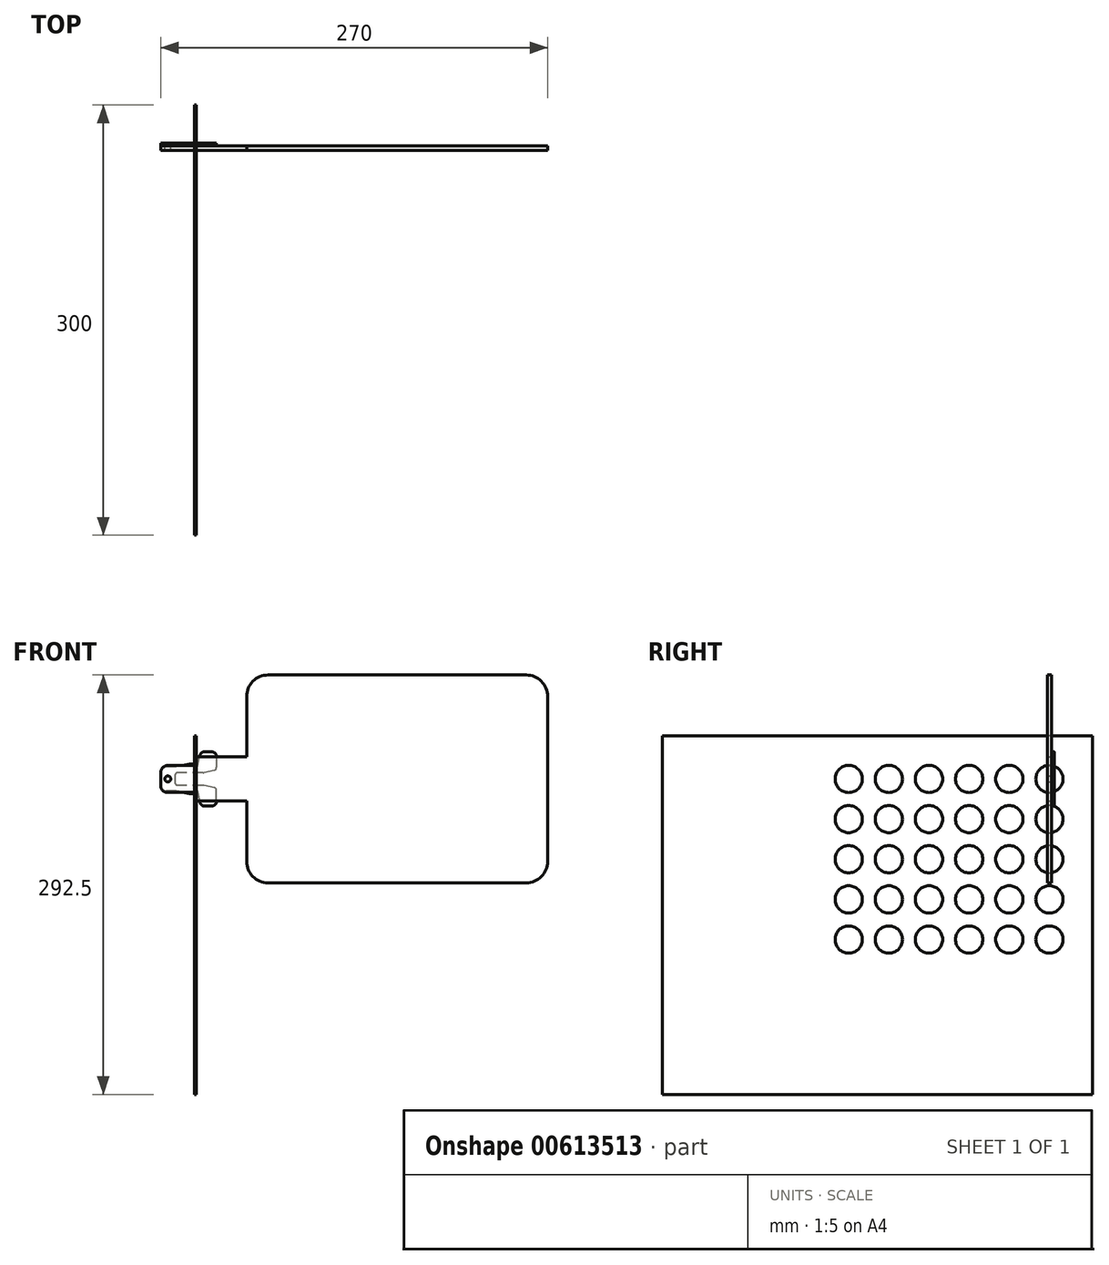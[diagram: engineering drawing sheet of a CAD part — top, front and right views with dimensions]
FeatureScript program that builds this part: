
annotation { "Feature Type Name" : "Feature", "Feature Type Description" : "" }
export const myFeature = defineFeature(function(context is Context, id is Id, definition is map)
    precondition{}
    {
        {
            var Q0;
            Q0=qCreatedBy(makeId("Front.planeOp"),FACE);
            var sketch = newSketch(context, id + "F0", { "sketchPlane" : qUnion([Q0])});
            skLineSegment(sketch, "E0.bottom", {"start": v(90, -72.5) * mm, "end": v(-90, -72.5) * mm});
            skLineSegment(sketch, "E0.top", {"start": v(90, 72.5) * mm, "end": v(-90, 72.5) * mm});
            skLineSegment(sketch, "E0.left", {"start": v(105, -57.5) * mm, "end": v(105, 57.5) * mm});
            skLineSegment(sketch, "E0.right", {"start": v(-105, -57.5) * mm, "end": v(-105, -15.4) * mm});
            skPoint(sketch, "E0.middle", {"position": v(0, 0) * mm});
            skPoint(sketch, "E1.visualSharp", {"position": v(-105, 72.5) * mm});
            skArc(sketch, "E1.filletArc", {"start": v(-90, 72.5) * mm, "mid": v(-100.6, 68.1) * mm, "end": v(-105, 57.5) * mm});
            skPoint(sketch, "E2.visualSharp", {"position": v(105, 72.5) * mm});
            skArc(sketch, "E2.filletArc", {"start": v(105, 57.5) * mm, "mid": v(100.6, 68.1) * mm, "end": v(90, 72.5) * mm});
            skPoint(sketch, "E3.visualSharp", {"position": v(105, -72.5) * mm});
            skArc(sketch, "E3.filletArc", {"start": v(90, -72.5) * mm, "mid": v(100.6, -68.1) * mm, "end": v(105, -57.5) * mm});
            skPoint(sketch, "E4.visualSharp", {"position": v(-105, -72.5) * mm});
            skArc(sketch, "E4.filletArc", {"start": v(-105, -57.5) * mm, "mid": v(-100.6, -68.1) * mm, "end": v(-90, -72.5) * mm});
            skLineSegment(sketch, "E5", {"start": v(-165, 0) * mm, "end": v(-165, -4.4) * mm});
            skLineSegment(sketch, "E6", {"start": v(-160, -9.4) * mm, "end": v(-140, -9.4) * mm});
            skLineSegment(sketch, "E7", {"start": v(-140, -9.4) * mm, "end": v(-140, -15.4) * mm});
            skLineSegment(sketch, "E8", {"start": v(-140, -15.4) * mm, "end": v(-105, -15.4) * mm});
            skLineSegment(sketch, "E9.MirrorCS", {"start": v(-140, 15.4) * mm, "end": v(-105, 15.4) * mm});
            skLineSegment(sketch, "E10.MirrorCS", {"start": v(-140, 9.4) * mm, "end": v(-140, 15.4) * mm});
            skLineSegment(sketch, "E11.MirrorCS", {"start": v(-160, 9.4) * mm, "end": v(-140, 9.4) * mm});
            skLineSegment(sketch, "E12.MirrorCS", {"start": v(-165, 0) * mm, "end": v(-165, 4.4) * mm});
            skLineSegment(sketch, "E13.trimOffspring", {"start": v(-105, 15.4) * mm, "end": v(-105, 57.5) * mm});
            skCircle(sketch, "E14", {"center": v(-160, 0) * mm, "radius": 2.1 * mm});
            skPoint(sketch, "E15.visualSharp", {"position": v(-165, 9.4) * mm});
            skArc(sketch, "E15.filletArc", {"start": v(-160, 9.4) * mm, "mid": v(-163.54, 7.94) * mm, "end": v(-165, 4.4) * mm});
            skPoint(sketch, "E16.visualSharp", {"position": v(-165, -9.4) * mm});
            skArc(sketch, "E16.filletArc", {"start": v(-165, -4.4) * mm, "mid": v(-163.54, -7.94) * mm, "end": v(-160, -9.4) * mm});
            skSolve(sketch);
        }
        {
            var Q0;
            Q0=makeQuery(id+"F0.imprint","IMPRINT",FACE,{"disambiguationData":[TD([[makeQuery(id+"F0.imprint","IMPRINT",EDGE,{"derivedFrom":sQuery(id+"F0.wireOp",EDGE,"E0.bottom")}),-1.0]])]});
            extrude(context, id + "F1", {"entities" : qUnion([Q0]), "depth" : 3 * mm, "offsetDistance" : 25 * mm, "symmetric" : true});
        }
        {
            var Q0;
            Q0=makeQuery(id+"F1.opExtrude","SWEPT_FACE",FACE,{"disambiguationData":[OSD([sQuery(id+"F0.wireOp",EDGE,"E10.MirrorCS")])]});
            cPlane(context, id + "F2", {"entities" : qUnion([Q0]), "cplaneType" : CPlaneType.OFFSET, "offset" : 0 * mm, "width" : 150 * mm, "height" : 150 * mm});
        }
        {
            var Q0;
            Q0=qCreatedBy(id+"F2.planeOp",FACE);
            var sketch = newSketch(context, id + "F3", { "sketchPlane" : qUnion([Q0])});
            skCircle(sketch, "E17", {"center": v(0, 0) * mm, "radius": 9.5 * mm});
            skLineSegment(sketch, "E18.bottom", {"start": v(-30, 30) * mm, "end": v(270, 30) * mm});
            skLineSegment(sketch, "E18.top", {"start": v(-30, -220) * mm, "end": v(270, -220) * mm});
            skLineSegment(sketch, "E18.left", {"start": v(-30, 30) * mm, "end": v(-30, -220) * mm});
            skLineSegment(sketch, "E18.right", {"start": v(270, 30) * mm, "end": v(270, -220) * mm});
            skCircle(sketch, "E19.0.1.0", {"center": v(0, -28) * mm, "radius": 9.5 * mm});
            skCircle(sketch, "E19.0.2.0", {"center": v(0, -56) * mm, "radius": 9.5 * mm});
            skCircle(sketch, "E19.0.3.0", {"center": v(0, -84) * mm, "radius": 9.5 * mm});
            skCircle(sketch, "E19.0.4.0", {"center": v(0, -112) * mm, "radius": 9.5 * mm});
            skCircle(sketch, "E19.1.0.0", {"center": v(28, 0) * mm, "radius": 9.5 * mm});
            skCircle(sketch, "E19.1.1.0", {"center": v(28, -28) * mm, "radius": 9.5 * mm});
            skCircle(sketch, "E19.1.2.0", {"center": v(28, -56) * mm, "radius": 9.5 * mm});
            skCircle(sketch, "E19.1.3.0", {"center": v(28, -84) * mm, "radius": 9.5 * mm});
            skCircle(sketch, "E19.1.4.0", {"center": v(28, -112) * mm, "radius": 9.5 * mm});
            skCircle(sketch, "E19.2.0.0", {"center": v(56, 0) * mm, "radius": 9.5 * mm});
            skCircle(sketch, "E19.2.1.0", {"center": v(56, -28) * mm, "radius": 9.5 * mm});
            skCircle(sketch, "E19.2.2.0", {"center": v(56, -56) * mm, "radius": 9.5 * mm});
            skCircle(sketch, "E19.2.3.0", {"center": v(56, -84) * mm, "radius": 9.5 * mm});
            skCircle(sketch, "E19.2.4.0", {"center": v(56, -112) * mm, "radius": 9.5 * mm});
            skCircle(sketch, "E19.3.0.0", {"center": v(84, 0) * mm, "radius": 9.5 * mm});
            skCircle(sketch, "E19.3.1.0", {"center": v(84, -28) * mm, "radius": 9.5 * mm});
            skCircle(sketch, "E19.3.2.0", {"center": v(84, -56) * mm, "radius": 9.5 * mm});
            skCircle(sketch, "E19.3.3.0", {"center": v(84, -84) * mm, "radius": 9.5 * mm});
            skCircle(sketch, "E19.3.4.0", {"center": v(84, -112) * mm, "radius": 9.5 * mm});
            skCircle(sketch, "E19.4.0.0", {"center": v(112, 0) * mm, "radius": 9.5 * mm});
            skCircle(sketch, "E19.4.1.0", {"center": v(112, -28) * mm, "radius": 9.5 * mm});
            skCircle(sketch, "E19.4.2.0", {"center": v(112, -56) * mm, "radius": 9.5 * mm});
            skCircle(sketch, "E19.4.3.0", {"center": v(112, -84) * mm, "radius": 9.5 * mm});
            skCircle(sketch, "E19.4.4.0", {"center": v(112, -112) * mm, "radius": 9.5 * mm});
            skCircle(sketch, "E19.5.0.0", {"center": v(140, 0) * mm, "radius": 9.5 * mm});
            skCircle(sketch, "E19.5.1.0", {"center": v(140, -28) * mm, "radius": 9.5 * mm});
            skCircle(sketch, "E19.5.2.0", {"center": v(140, -56) * mm, "radius": 9.5 * mm});
            skCircle(sketch, "E19.5.3.0", {"center": v(140, -84) * mm, "radius": 9.5 * mm});
            skCircle(sketch, "E19.5.4.0", {"center": v(140, -112) * mm, "radius": 9.5 * mm});
            skLineSegment(sketch, "E19.direction1", {"start": v(0, 0) * mm, "end": v(28, 0) * mm, "construction": true});
            skLineSegment(sketch, "E19.direction2", {"start": v(0, 0) * mm, "end": v(0, -28) * mm, "construction": true});
            skSolve(sketch);
        }
        {
            var Q0;
            Q0=qSketchRegion(id+"F3",true);
            extrude(context, id + "F4", {"entities" : qUnion([Q0]), "depth" : 1.5 * mm, "offsetDistance" : 25 * mm});
        }
        {
            var Q0;
            Q0=makeQuery(id+"F1.opExtrude","CAP_FACE",FACE,{"disambiguationData":[OSD([sQuery(id+"F0.wireOp",EDGE,"E0.bottom"),sQuery(id+"F0.wireOp",EDGE,"E0.top"),sQuery(id+"F0.wireOp",EDGE,"E0.left"),sQuery(id+"F0.wireOp",EDGE,"E0.right"),sQuery(id+"F0.wireOp",EDGE,"E1.filletArc"),sQuery(id+"F0.wireOp",EDGE,"E2.filletArc"),sQuery(id+"F0.wireOp",EDGE,"E3.filletArc"),sQuery(id+"F0.wireOp",EDGE,"E4.filletArc"),sQuery(id+"F0.wireOp",EDGE,"E5"),sQuery(id+"F0.wireOp",EDGE,"E6"),sQuery(id+"F0.wireOp",EDGE,"E7"),sQuery(id+"F0.wireOp",EDGE,"E8"),sQuery(id+"F0.wireOp",EDGE,"E9.MirrorCS"),sQuery(id+"F0.wireOp",EDGE,"E10.MirrorCS"),sQuery(id+"F0.wireOp",EDGE,"E11.MirrorCS"),sQuery(id+"F0.wireOp",EDGE,"E12.MirrorCS"),sQuery(id+"F0.wireOp",EDGE,"E13.trimOffspring"),sQuery(id+"F0.wireOp",EDGE,"E14")])],"isStart":true});
            var sketch = newSketch(context, id + "F5", { "sketchPlane" : qUnion([Q0])});
            skLineSegment(sketch, "E20", {"start": v(139.5, 7.9) * mm, "end": v(141.5, 7.9) * mm});
            skLineSegment(sketch, "E21", {"start": v(141.5, 7.9) * mm, "end": v(142, 10.4) * mm});
            skLineSegment(sketch, "E22", {"start": v(142, 10.4) * mm, "end": v(145, 10.4) * mm});
            skLineSegment(sketch, "E23", {"start": v(139.5, 7.9) * mm, "end": v(137.56, 16.42) * mm});
            skLineSegment(sketch, "E24", {"start": v(134.46, 18.9) * mm, "end": v(129.3, 18.9) * mm});
            skLineSegment(sketch, "E25", {"start": v(126, 15.6) * mm, "end": v(126, 8) * mm});
            skLineSegment(sketch, "E26", {"start": v(127.57, 6.05) * mm, "end": v(134.79, 4.45) * mm});
            skLineSegment(sketch, "E27", {"start": v(135.22, 4.4) * mm, "end": v(153, 4.4) * mm});
            skLineSegment(sketch, "E28", {"start": v(155, 2.4) * mm, "end": v(155, 0) * mm});
            skArc(sketch, "E29", {"start": v(129.3, 18.9) * mm, "mid": v(126.97, 17.93) * mm, "end": v(126, 15.6) * mm});
            skArc(sketch, "E30", {"start": v(137.56, 16.42) * mm, "mid": v(136.44, 18.2) * mm, "end": v(134.46, 18.9) * mm});
            skPoint(sketch, "E31.orphan", {"position": v(137, 18.9) * mm});
            skCircle(sketch, "E32.0", {"center": v(160, 0) * mm, "radius": 2.1 * mm});
            skPoint(sketch, "E33.visualSharp", {"position": v(126, 6.4) * mm});
            skArc(sketch, "E33.filletArc", {"start": v(126, 8) * mm, "mid": v(126.44, 6.75) * mm, "end": v(127.57, 6.05) * mm});
            skPoint(sketch, "E34.visualSharp", {"position": v(155, 4.4) * mm});
            skArc(sketch, "E34.filletArc", {"start": v(155, 2.4) * mm, "mid": v(154.41, 3.81) * mm, "end": v(153, 4.4) * mm});
            skPoint(sketch, "E35.visualSharp", {"position": v(135, 4.4) * mm});
            skArc(sketch, "E35.filletArc", {"start": v(134.79, 4.45) * mm, "mid": v(135, 4.41) * mm, "end": v(135.22, 4.4) * mm});
            skLineSegment(sketch, "E36", {"start": v(145, 10.4) * mm, "end": v(154, 8.4) * mm});
            skLineSegment(sketch, "E37", {"start": v(154, 8.4) * mm, "end": v(161, 8.4) * mm});
            skLineSegment(sketch, "E38", {"start": v(165, 4.4) * mm, "end": v(165, 0) * mm});
            skPoint(sketch, "E39.visualSharp", {"position": v(165, 8.4) * mm});
            skArc(sketch, "E39.filletArc", {"start": v(165, 4.4) * mm, "mid": v(163.83, 7.23) * mm, "end": v(161, 8.4) * mm});
            skLineSegment(sketch, "E40.MirrorCS", {"start": v(155, -2.4) * mm, "end": v(155, 0) * mm});
            skArc(sketch, "E41.MirrorCS", {"start": v(155, -2.4) * mm, "mid": v(154.41, -3.81) * mm, "end": v(153, -4.4) * mm});
            skLineSegment(sketch, "E42.MirrorCS", {"start": v(135.22, -4.4) * mm, "end": v(153, -4.4) * mm});
            skArc(sketch, "E43.MirrorCS", {"start": v(134.79, -4.45) * mm, "mid": v(135, -4.41) * mm, "end": v(135.22, -4.4) * mm});
            skLineSegment(sketch, "E44.MirrorCS", {"start": v(127.57, -6.05) * mm, "end": v(134.79, -4.45) * mm});
            skArc(sketch, "E45.MirrorCS", {"start": v(126, -8) * mm, "mid": v(126.44, -6.75) * mm, "end": v(127.57, -6.05) * mm});
            skLineSegment(sketch, "E46.MirrorCS", {"start": v(126, -15.6) * mm, "end": v(126, -8) * mm});
            skArc(sketch, "E47.MirrorCS", {"start": v(129.3, -18.9) * mm, "mid": v(126.97, -17.93) * mm, "end": v(126, -15.6) * mm});
            skLineSegment(sketch, "E48.MirrorCS", {"start": v(134.46, -18.9) * mm, "end": v(129.3, -18.9) * mm});
            skArc(sketch, "E49.MirrorCS", {"start": v(137.56, -16.42) * mm, "mid": v(136.44, -18.2) * mm, "end": v(134.46, -18.9) * mm});
            skLineSegment(sketch, "E50.MirrorCS", {"start": v(139.5, -7.9) * mm, "end": v(137.56, -16.42) * mm});
            skLineSegment(sketch, "E51.MirrorCS", {"start": v(139.5, -7.9) * mm, "end": v(141.5, -7.9) * mm});
            skLineSegment(sketch, "E52.MirrorCS", {"start": v(141.5, -7.9) * mm, "end": v(142, -10.4) * mm});
            skLineSegment(sketch, "E53.MirrorCS", {"start": v(142, -10.4) * mm, "end": v(145, -10.4) * mm});
            skLineSegment(sketch, "E54.MirrorCS", {"start": v(145, -10.4) * mm, "end": v(154, -8.4) * mm});
            skLineSegment(sketch, "E55.MirrorCS", {"start": v(154, -8.4) * mm, "end": v(161, -8.4) * mm});
            skArc(sketch, "E56.MirrorCS", {"start": v(165, -4.4) * mm, "mid": v(163.83, -7.23) * mm, "end": v(161, -8.4) * mm});
            skLineSegment(sketch, "E57.MirrorCS", {"start": v(165, -4.4) * mm, "end": v(165, 0) * mm});
            skSolve(sketch);
        }
        {
            var Q0;
            Q0=qSketchRegion(id+"F5",true);
            extrude(context, id + "F6", {"entities" : qUnion([Q0]), "depth" : 2 * mm, "offsetDistance" : 25 * mm});
        }
    });
